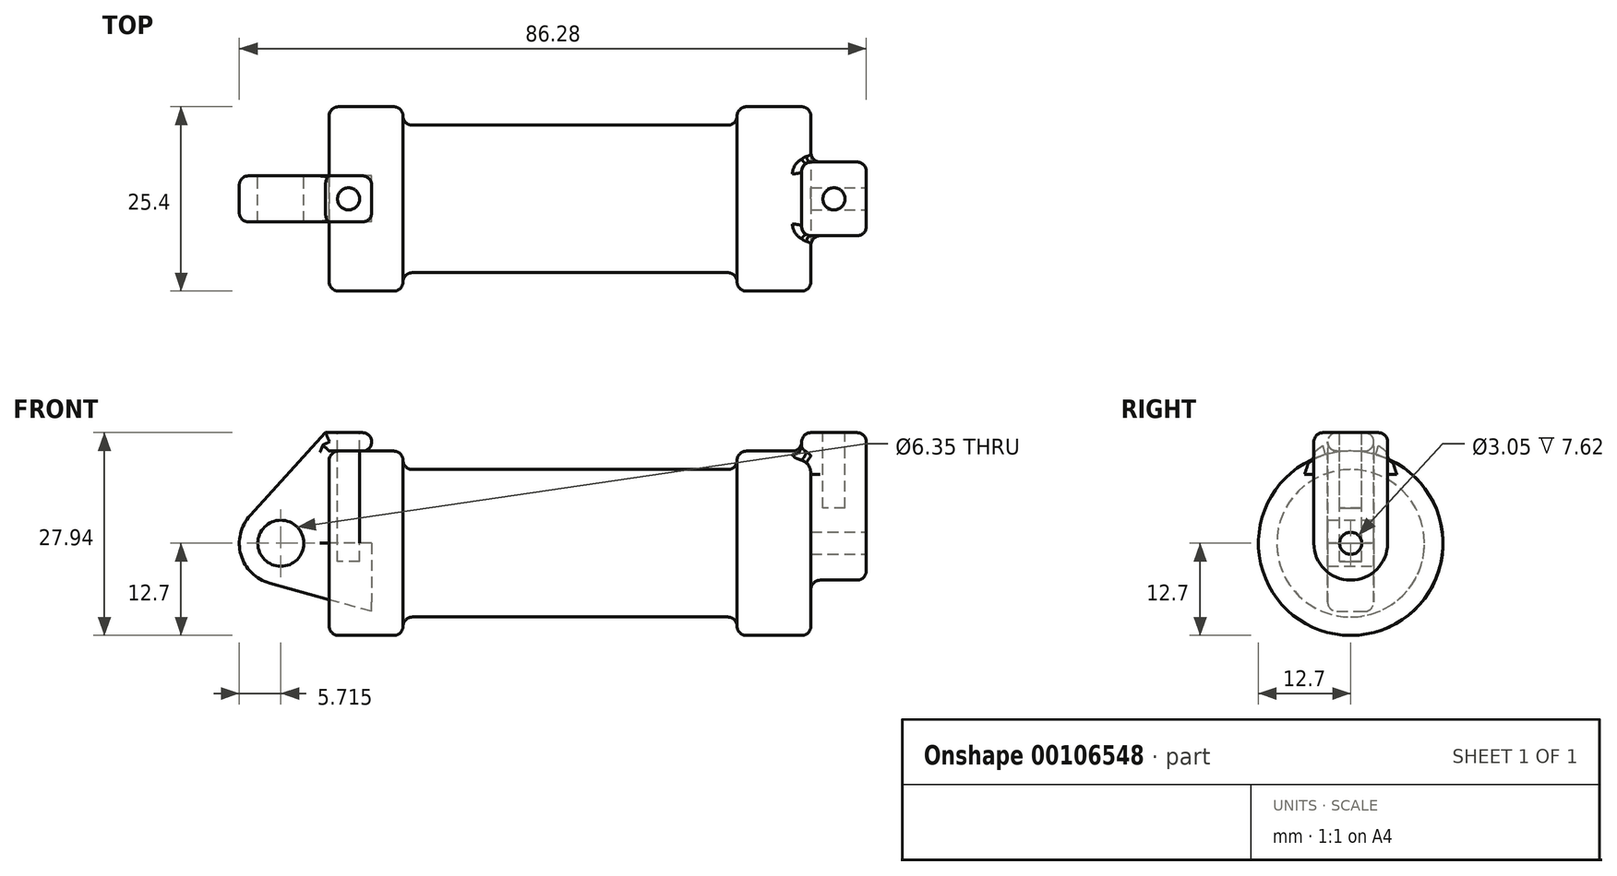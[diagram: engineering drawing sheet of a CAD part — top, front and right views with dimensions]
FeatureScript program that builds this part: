
annotation { "Feature Type Name" : "Feature", "Feature Type Description" : "" }
export const myFeature = defineFeature(function(context is Context, id is Id, definition is map)
    precondition{}
    {
        {
            var Q0;
            Q0=qCreatedBy(makeId("Front.planeOp"),FACE);
            var sketch = newSketch(context, id + "F0", { "sketchPlane" : qUnion([Q0])});
            skLineSegment(sketch, "E0", {"start": v(0, 0) * mm, "end": v(0, 12.7) * mm});
            skLineSegment(sketch, "E1", {"start": v(0, 12.7) * mm, "end": v(10.16, 12.7) * mm});
            skLineSegment(sketch, "E2", {"start": v(10.16, 12.7) * mm, "end": v(10.16, 10.16) * mm});
            skLineSegment(sketch, "E3", {"start": v(10.16, 10.16) * mm, "end": v(56.13, 10.16) * mm});
            skLineSegment(sketch, "E4", {"start": v(56.13, 10.16) * mm, "end": v(56.13, 12.7) * mm});
            skLineSegment(sketch, "E5", {"start": v(56.13, 12.7) * mm, "end": v(66.3, 12.7) * mm});
            skLineSegment(sketch, "E6", {"start": v(66.3, 12.7) * mm, "end": v(66.3, 0) * mm});
            skLineSegment(sketch, "E7", {"start": v(66.3, 0) * mm, "end": v(0, 0) * mm});
            skLineSegment(sketch, "E8", {"start": v(5.84, 15.24) * mm, "end": v(-0.5, 15.24) * mm});
            skLineSegment(sketch, "E9", {"start": v(-0.5, 15.24) * mm, "end": v(-10.88, 3.85) * mm});
            skLineSegment(sketch, "E10", {"start": v(0, 0) * mm, "end": v(-6.65, 0) * mm});
            skCircle(sketch, "E11", {"center": v(-6.65, 0) * mm, "radius": 5.72 * mm});
            skCircle(sketch, "E12", {"center": v(-6.65, 0) * mm, "radius": 3.18 * mm});
            skLineSegment(sketch, "E13", {"start": v(5.84, 15.24) * mm, "end": v(5.84, -9.4) * mm});
            skLineSegment(sketch, "E14", {"start": v(5.84, -9.4) * mm, "end": v(-8.18, -5.5) * mm});
            skSolve(sketch);
        }
        {
            var Q0;
            {var subQ0=sQuery(id+"F0.wireOp",EDGE,"E2");Q0=makeQuery(id+"F0.imprint","IMPRINT",FACE,{"disambiguationData":[TD([[makeQuery(id+"F0.imprint","IMPRINT",EDGE,{"derivedFrom":subQ0}),-1.0]])]});}
            var Q1;
            {var subQ0=sQuery(id+"F0.wireOp",EDGE,"E0");Q1=makeQuery(id+"F0.imprint","IMPRINT",FACE,{"disambiguationData":[TD([[makeQuery(id+"F0.imprint","IMPRINT",EDGE,{"derivedFrom":subQ0}),-1.0]])]});}
            var Q2;
            Q2=sQuery(id+"F0.wireOp",EDGE,"E7");
            revolve(context, id + "F1", {"entities" : qUnion([Q0, Q1]), "axis" : qUnion([Q2]), "revolveType" : RevolveType.FULL});
        }
        {
            var Q0;
            {var subQ3=sQuery(id+"F0.wireOp",EDGE,"E0");Q0=makeQuery(id+"F0.imprint","IMPRINT",FACE,{"disambiguationData":[TD([[makeQuery(id+"F0.imprint","IMPRINT",EDGE,{"derivedFrom":subQ3}),1.0]])]});}
            var Q1;
            {var subQ4=sQuery(id+"F0.wireOp",EDGE,"E12");Q1=makeQuery(id+"F0.imprint","IMPRINT",FACE,{"disambiguationData":[TD([[makeQuery(id+"F0.imprint","IMPRINT",EDGE,{"derivedFrom":subQ4}),-1.0]])]});}
            var Q2;
            {var subQ0=sQuery(id+"F0.wireOp",EDGE,"E14");Q2=makeQuery(id+"F0.imprint","IMPRINT",FACE,{"disambiguationData":[TD([[makeQuery(id+"F0.imprint","IMPRINT",EDGE,{"derivedFrom":subQ0}),-1.0]])]});}
            extrude(context, id + "F2", {"entities" : qUnion([Q0, Q1, Q2]), "endBound" : BoundingType.SYMMETRIC, "depth" : 6.35 * mm});
        }
        {
            var Q0;
            Q0=makeQuery(id+"F1.opRevolve","SWEPT_FACE",FACE,{"disambiguationData":[OSD([sQuery(id+"F0.wireOp",EDGE,"E6")])]});
            var sketch = newSketch(context, id + "F3", { "sketchPlane" : qUnion([Q0])});
            skCircle(sketch, "E15", {"center": v(0, 0) * mm, "radius": 1.52 * mm});
            skCircle(sketch, "E16", {"center": v(0, 0) * mm, "radius": 5.08 * mm});
            skLineSegment(sketch, "E17", {"start": v(5.08, 0) * mm, "end": v(5.08, 15.24) * mm});
            skLineSegment(sketch, "E18", {"start": v(-5.08, 0) * mm, "end": v(-5.08, 15.24) * mm});
            skLineSegment(sketch, "E19", {"start": v(-5.08, 15.24) * mm, "end": v(5.08, 15.24) * mm});
            skSolve(sketch);
        }
        {
            var Q0;
            {var subQ0=sQuery(id+"F3.wireOp",EDGE,"E19");Q0=makeQuery(id+"F3.imprint","IMPRINT",FACE,{"disambiguationData":[TD([[makeQuery(id+"F3.imprint","IMPRINT",EDGE,{"derivedFrom":subQ0}),-1.0]])]});}
            var Q1;
            {var subQ0=sQuery(id+"F3.wireOp",EDGE,"E17");var subQ1=sQuery(id+"F3.wireOp",EDGE,"E16");var subQ2=makeQuery(id+"F3.imprint","INTERSECT",VERTEX,{"derivedFrom":[subQ1,subQ0]});Q1=makeQuery(id+"F3.imprint","IMPRINT",FACE,{"disambiguationData":[TD([[makeQuery(id+"F3.imprint","IMPRINT",EDGE,{"disambiguationData":[TD([[subQ2,-1.0]])],"derivedFrom":subQ1}),-1.0]])]});}
            var Q2;
            Q2=makeQuery(id+"F3.imprint","IMPRINT",FACE,{"disambiguationData":[TD([[makeQuery(id+"F3.imprint","IMPRINT",EDGE,{"derivedFrom":sQuery(id+"F3.wireOp",EDGE,"E15")}),-1.0]])]});
            extrude(context, id + "F4", {"entities" : qUnion([Q0, Q1, Q2]), "operationType" : NewBodyOperationType.ADD, "oppositeDirection" : true, "depth" : 1.27 * mm, "hasSecondDirection" : true, "secondDirectionOppositeDirection" : false, "secondDirectionDepth" : 7.62 * mm});
        }
        {
            var Q0;
            Q0=makeQuery(id+"F4.opExtrude","SWEPT_FACE",FACE,{"disambiguationData":[OSD([sQuery(id+"F3.wireOp",EDGE,"E19")])]});
            var sketch = newSketch(context, id + "F5", { "sketchPlane" : qUnion([Q0])});
            skCircle(sketch, "E20", {"center": v(69.47, 0) * mm, "radius": 1.52 * mm});
            skPoint(sketch, "E20.centerSnap0", {"position": v(65.02, 0) * mm});
            skPoint(sketch, "E20.centerSnap1", {"position": v(69.47, 5.08) * mm});
            skSolve(sketch);
        }
        {
            var Q0;
            Q0=makeQuery(id+"F5.imprint","IMPRINT",FACE,{"disambiguationData":[TD([[makeQuery(id+"F5.imprint","IMPRINT",EDGE,{"derivedFrom":sQuery(id+"F5.wireOp",EDGE,"E20")}),1.0]])]});
            extrude(context, id + "F6", {"entities" : qUnion([Q0]), "oppositeDirection" : true, "depth" : 10.4 * mm});
        }
        {
            var Q0;
            Q0=makeQuery(id+"F2.opExtrude","SWEPT_FACE",FACE,{"disambiguationData":[OSD([sQuery(id+"F0.wireOp",EDGE,"E8")])]});
            var sketch = newSketch(context, id + "F7", { "sketchPlane" : qUnion([Q0])});
            skCircle(sketch, "E21", {"center": v(2.67, 0) * mm, "radius": 1.52 * mm});
            skPoint(sketch, "E21.centerSnap0", {"position": v(2.67, 3.18) * mm});
            skPoint(sketch, "E21.centerSnap1", {"position": v(5.84, 0) * mm});
            skSolve(sketch);
        }
        {
            var Q0;
            Q0=makeQuery(id+"F7.imprint","IMPRINT",FACE,{"disambiguationData":[TD([[makeQuery(id+"F7.imprint","IMPRINT",EDGE,{"derivedFrom":sQuery(id+"F7.wireOp",EDGE,"E21")}),1.0]])]});
            extrude(context, id + "F8", {"entities" : qUnion([Q0]), "oppositeDirection" : true, "depth" : 17.78 * mm});
        }
        {
            var Q0;
            Q0=makeQuery(id+"F1.opRevolve","SWEPT_EDGE",EDGE,{"disambiguationData":[OSD([sQuery(id+"F0.wireOp",EDGE,"E0"),sQuery(id+"F0.wireOp",EDGE,"E1")])]});
            var Q1;
            Q1=makeQuery(id+"F1.opRevolve","SWEPT_EDGE",EDGE,{"disambiguationData":[OSD([sQuery(id+"F0.wireOp",EDGE,"E5"),sQuery(id+"F0.wireOp",EDGE,"E6")])]});
            var Q2;
            Q2=makeQuery(id+"F1.opRevolve","SWEPT_EDGE",EDGE,{"disambiguationData":[OSD([sQuery(id+"F0.wireOp",EDGE,"E1"),sQuery(id+"F0.wireOp",EDGE,"E2")])]});
            var Q3;
            Q3=makeQuery(id+"F1.opRevolve","SWEPT_EDGE",EDGE,{"disambiguationData":[OSD([sQuery(id+"F0.wireOp",EDGE,"E4"),sQuery(id+"F0.wireOp",EDGE,"E5")])]});
            var Q4;
            Q4=makeQuery(id+"F1.opRevolve","SWEPT_EDGE",EDGE,{"disambiguationData":[OSD([sQuery(id+"F0.wireOp",EDGE,"E2"),sQuery(id+"F0.wireOp",EDGE,"E3")])]});
            var Q5;
            Q5=makeQuery(id+"F1.opRevolve","SWEPT_EDGE",EDGE,{"disambiguationData":[OSD([sQuery(id+"F0.wireOp",EDGE,"E3"),sQuery(id+"F0.wireOp",EDGE,"E4")])]});
            fillet(context, id + "F9", {"entities" : qUnion([Q0, Q1, Q2, Q3, Q4, Q5]), "radius" : 1.27 * mm, "tangentPropagation" : true, "allowEdgeOverflow" : false});
        }
        {
            var Q0;
            Q0=makeQuery(id+"F2.opExtrude","CAP_EDGE",EDGE,{"disambiguationData":[OSD([sQuery(id+"F0.wireOp",EDGE,"E1")])],"isStart":false});
            var Q1;
            Q1=makeQuery(id+"F2.opExtrude","CAP_EDGE",EDGE,{"disambiguationData":[OSD([sQuery(id+"F0.wireOp",EDGE,"E9")])],"isStart":false});
            var Q2;
            Q2=makeQuery(id+"F2.opExtrude","CAP_EDGE",EDGE,{"disambiguationData":[OSD([sQuery(id+"F0.wireOp",EDGE,"E9")])],"isStart":true});
            var Q3;
            Q3=makeQuery(id+"F2.opExtrude","CAP_EDGE",EDGE,{"disambiguationData":[OSD([sQuery(id+"F0.wireOp",EDGE,"E11")])],"isStart":false});
            var Q4;
            Q4=makeQuery(id+"F2.opExtrude","CAP_EDGE",EDGE,{"disambiguationData":[OSD([sQuery(id+"F0.wireOp",EDGE,"E11")])],"isStart":true});
            var Q5;
            Q5=makeQuery(id+"F2.opExtrude","CAP_EDGE",EDGE,{"disambiguationData":[OSD([sQuery(id+"F0.wireOp",EDGE,"E14")])],"isStart":false});
            var Q6;
            Q6=makeQuery(id+"F2.opExtrude","CAP_EDGE",EDGE,{"disambiguationData":[OSD([sQuery(id+"F0.wireOp",EDGE,"E14")])],"isStart":true});
            var Q7;
            Q7=makeQuery(id+"F2.opExtrude","CAP_EDGE",EDGE,{"disambiguationData":[OSD([sQuery(id+"F0.wireOp",EDGE,"E0")])],"isStart":true});
            var Q8;
            Q8=makeQuery(id+"F2.opExtrude","CAP_EDGE",EDGE,{"disambiguationData":[OSD([sQuery(id+"F0.wireOp",EDGE,"E0")])],"isStart":false});
            var Q9;
            Q9=makeQuery(id+"F2.opExtrude","CAP_EDGE",EDGE,{"disambiguationData":[OSD([sQuery(id+"F0.wireOp",EDGE,"E8")])],"isStart":false});
            var Q10;
            {var subQ0=sQuery(id+"F0.wireOp",EDGE,"E13");Q10=makeQuery(id+"F2.opExtrude","CAP_EDGE",EDGE,{"disambiguationData":[OSD([subQ0]),TDD([makeQuery(id+"F0.imprint","IMPRINT",EDGE,{"disambiguationData":[TD([[makeQuery(id+"F0.imprint","INTERSECT",VERTEX,{"derivedFrom":[sQuery(id+"F0.wireOp",EDGE,"E8"),subQ0]}),-1.0]])],"derivedFrom":subQ0})])],"isStart":false});}
            var Q11;
            Q11=makeQuery(id+"F2.opExtrude","CAP_EDGE",EDGE,{"disambiguationData":[OSD([sQuery(id+"F0.wireOp",EDGE,"E1")])],"isStart":true});
            var Q12;
            {var subQ0=sQuery(id+"F0.wireOp",EDGE,"E13");Q12=makeQuery(id+"F2.opExtrude","CAP_EDGE",EDGE,{"disambiguationData":[OSD([subQ0]),TDD([makeQuery(id+"F0.imprint","IMPRINT",EDGE,{"disambiguationData":[TD([[makeQuery(id+"F0.imprint","INTERSECT",VERTEX,{"derivedFrom":[sQuery(id+"F0.wireOp",EDGE,"E8"),subQ0]}),-1.0]])],"derivedFrom":subQ0})])],"isStart":true});}
            var Q13;
            Q13=makeQuery(id+"F2.opExtrude","SWEPT_EDGE",EDGE,{"disambiguationData":[OSD([sQuery(id+"F0.wireOp",EDGE,"E1"),sQuery(id+"F0.wireOp",EDGE,"E13")])]});
            var Q14;
            Q14=makeQuery(id+"F2.opExtrude","CAP_EDGE",EDGE,{"disambiguationData":[OSD([sQuery(id+"F0.wireOp",EDGE,"E8")])],"isStart":true});
            var Q15;
            Q15=makeQuery(id+"F2.opExtrude","SWEPT_EDGE",EDGE,{"disambiguationData":[OSD([sQuery(id+"F0.wireOp",EDGE,"E8"),sQuery(id+"F0.wireOp",EDGE,"E13")])]});
            fillet(context, id + "F10", {"entities" : qUnion([Q0, Q1, Q2, Q3, Q4, Q5, Q6, Q7, Q8, Q9, Q10, Q11, Q12, Q13, Q14, Q15]), "radius" : 1.27 * mm, "tangentPropagation" : true, "allowEdgeOverflow" : false});
        }
        {
            var Q0;
            Q0=makeQuery(id+"F4.opExtrude","CAP_EDGE",EDGE,{"disambiguationData":[OSD([sQuery(id+"F3.wireOp",EDGE,"E18")])],"isStart":false});
            var Q1;
            Q1=makeQuery(id+"F4.opExtrude","CAP_EDGE",EDGE,{"disambiguationData":[OSD([sQuery(id+"F3.wireOp",EDGE,"E18")])],"isStart":true});
            var Q2;
            Q2=makeQuery(id+"F4.opExtrude","CAP_EDGE",EDGE,{"disambiguationData":[OSD([sQuery(id+"F3.wireOp",EDGE,"E16")])],"isStart":true});
            var Q3;
            Q3=makeQuery(id+"F4.opExtrude","CAP_EDGE",EDGE,{"disambiguationData":[OSD([sQuery(id+"F3.wireOp",EDGE,"E17")])],"isStart":true});
            var Q4;
            Q4=makeQuery(id+"F4.opExtrude","CAP_EDGE",EDGE,{"disambiguationData":[OSD([sQuery(id+"F3.wireOp",EDGE,"E19")])],"isStart":true});
            var Q5;
            Q5=makeQuery(id+"F4.opExtrude","SWEPT_EDGE",EDGE,{"disambiguationData":[OSD([sQuery(id+"F3.wireOp",EDGE,"E17"),sQuery(id+"F3.wireOp",EDGE,"E19")])]});
            var Q6;
            Q6=makeQuery(id+"F4.opExtrude","CAP_EDGE",EDGE,{"disambiguationData":[OSD([sQuery(id+"F3.wireOp",EDGE,"E19")])],"isStart":false});
            var Q7;
            Q7=makeQuery(id+"F4.opExtrude","SWEPT_EDGE",EDGE,{"disambiguationData":[OSD([sQuery(id+"F3.wireOp",EDGE,"E18"),sQuery(id+"F3.wireOp",EDGE,"E19")])]});
            var Q8;
            Q8=makeQuery(id+"F4.boolean.opBoolean","INTERSECT",EDGE,{"derivedFrom":[makeQuery(id+"F1.opRevolve","SWEPT_FACE",FACE,{"disambiguationData":[OSD([sQuery(id+"F0.wireOp",EDGE,"E6")])]}),makeQuery(id+"F4.opExtrude","SWEPT_FACE",FACE,{"disambiguationData":[OSD([sQuery(id+"F3.wireOp",EDGE,"E18")])]})]});
            var Q9;
            Q9=makeQuery(id+"F4.boolean.opBoolean","INTERSECT",EDGE,{"derivedFrom":[makeQuery(id+"F1.opRevolve","SWEPT_FACE",FACE,{"disambiguationData":[OSD([sQuery(id+"F0.wireOp",EDGE,"E6")])]}),makeQuery(id+"F4.opExtrude","SWEPT_FACE",FACE,{"disambiguationData":[OSD([sQuery(id+"F3.wireOp",EDGE,"E16")])]})]});
            var Q10;
            Q10=makeQuery(id+"F4.boolean.opBoolean","INTERSECT",EDGE,{"derivedFrom":[makeQuery(id+"F1.opRevolve","SWEPT_FACE",FACE,{"disambiguationData":[OSD([sQuery(id+"F0.wireOp",EDGE,"E6")])]}),makeQuery(id+"F4.opExtrude","SWEPT_FACE",FACE,{"disambiguationData":[OSD([sQuery(id+"F3.wireOp",EDGE,"E17")])]})]});
            var Q11;
            Q11=makeQuery(id+"F4.opExtrude","CAP_EDGE",EDGE,{"disambiguationData":[OSD([sQuery(id+"F3.wireOp",EDGE,"E17")])],"isStart":false});
            var Q12;
            Q12=makeQuery(id+"F9.opFillet","BLEND_EDGE",EDGE,{"blendedFrom":[makeQuery(id+"F1.opRevolve","SWEPT_EDGE",EDGE,{"disambiguationData":[OSD([sQuery(id+"F0.wireOp",EDGE,"E5"),sQuery(id+"F0.wireOp",EDGE,"E6")])]}),makeQuery(id+"F4.opExtrude","SWEPT_FACE",FACE,{"disambiguationData":[OSD([sQuery(id+"F3.wireOp",EDGE,"E17")])]})],"blendedInto":[makeQuery(id+"F4.opExtrude","SWEPT_FACE",FACE,{"disambiguationData":[OSD([sQuery(id+"F3.wireOp",EDGE,"E17")])]})]});
            var Q13;
            Q13=makeQuery(id+"F9.opFillet","BLEND_EDGE",EDGE,{"blendedFrom":[makeQuery(id+"F1.opRevolve","SWEPT_EDGE",EDGE,{"disambiguationData":[OSD([sQuery(id+"F0.wireOp",EDGE,"E5"),sQuery(id+"F0.wireOp",EDGE,"E6")])]}),makeQuery(id+"F4.opExtrude","SWEPT_FACE",FACE,{"disambiguationData":[OSD([sQuery(id+"F3.wireOp",EDGE,"E18")])]})],"blendedInto":[makeQuery(id+"F4.opExtrude","SWEPT_FACE",FACE,{"disambiguationData":[OSD([sQuery(id+"F3.wireOp",EDGE,"E18")])]})]});
            var Q14;
            Q14=makeQuery(id+"F4.boolean.opBoolean","INTERSECT",EDGE,{"derivedFrom":[makeQuery(id+"F1.opRevolve","SWEPT_FACE",FACE,{"disambiguationData":[OSD([sQuery(id+"F0.wireOp",EDGE,"E5")])]}),makeQuery(id+"F4.opExtrude","CAP_FACE",FACE,{"disambiguationData":[OSD([sQuery(id+"F3.wireOp",EDGE,"E15"),sQuery(id+"F3.wireOp",EDGE,"E16"),sQuery(id+"F3.wireOp",EDGE,"E17"),sQuery(id+"F3.wireOp",EDGE,"E18"),sQuery(id+"F3.wireOp",EDGE,"E19")])],"isStart":false})]});
            fillet(context, id + "F11", {"entities" : qUnion([Q0, Q1, Q2, Q3, Q4, Q5, Q6, Q7, Q8, Q9, Q10, Q11, Q12, Q13, Q14]), "radius" : 1.27 * mm, "tangentPropagation" : true, "allowEdgeOverflow" : false});
        }
    });
